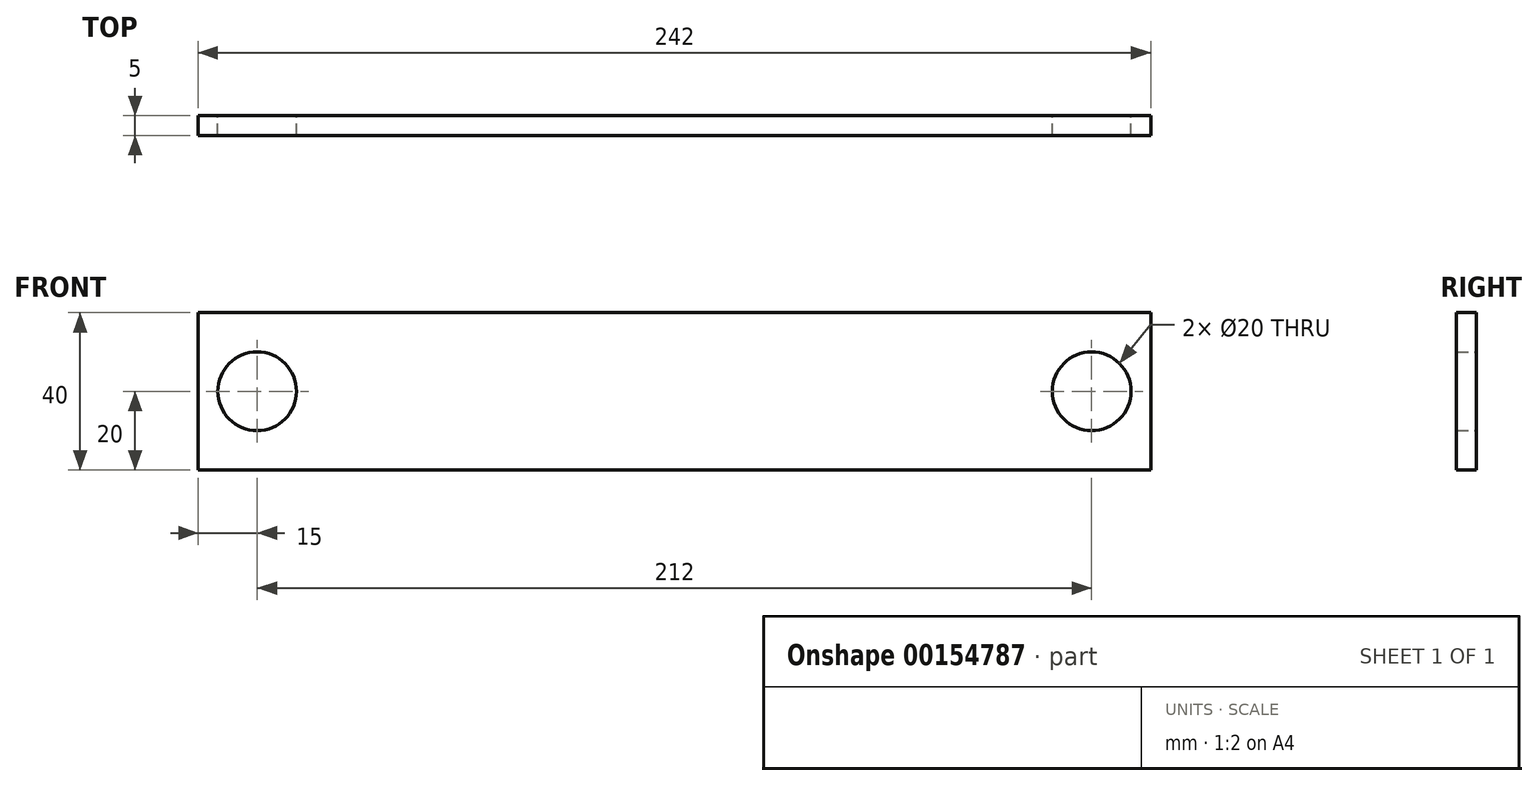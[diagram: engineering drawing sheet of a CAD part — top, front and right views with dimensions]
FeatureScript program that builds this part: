
annotation { "Feature Type Name" : "Feature", "Feature Type Description" : "" }
export const myFeature = defineFeature(function(context is Context, id is Id, definition is map)
    precondition{}
    {
        {
            var Q0;
            Q0=qCreatedBy(makeId("Front.planeOp"),FACE);
            var sketch = newSketch(context, id + "F0", { "sketchPlane" : qUnion([Q0])});
            skLineSegment(sketch, "E0.bottom", {"start": v(0, 0) * mm, "end": v(242, 0) * mm});
            skLineSegment(sketch, "E0.top", {"start": v(0, 40) * mm, "end": v(242, 40) * mm});
            skLineSegment(sketch, "E0.left", {"start": v(0, 0) * mm, "end": v(0, 40) * mm});
            skLineSegment(sketch, "E0.right", {"start": v(242, 0) * mm, "end": v(242, 40) * mm});
            skCircle(sketch, "E1", {"center": v(15, 20) * mm, "radius": 10 * mm});
            skPoint(sketch, "E1.centerSnap0", {"position": v(0, 20) * mm});
            skCircle(sketch, "E2", {"center": v(227, 20) * mm, "radius": 10 * mm});
            skPoint(sketch, "E2.centerSnap0", {"position": v(242, 20) * mm});
            skSolve(sketch);
        }
        {
            var Q0;
            Q0 = qSketchRegion(id + "F0", true);
            extrude(context, id + "F1", {"entities" : qUnion([Q0]), "depth" : 5 * mm});
        }
    });
